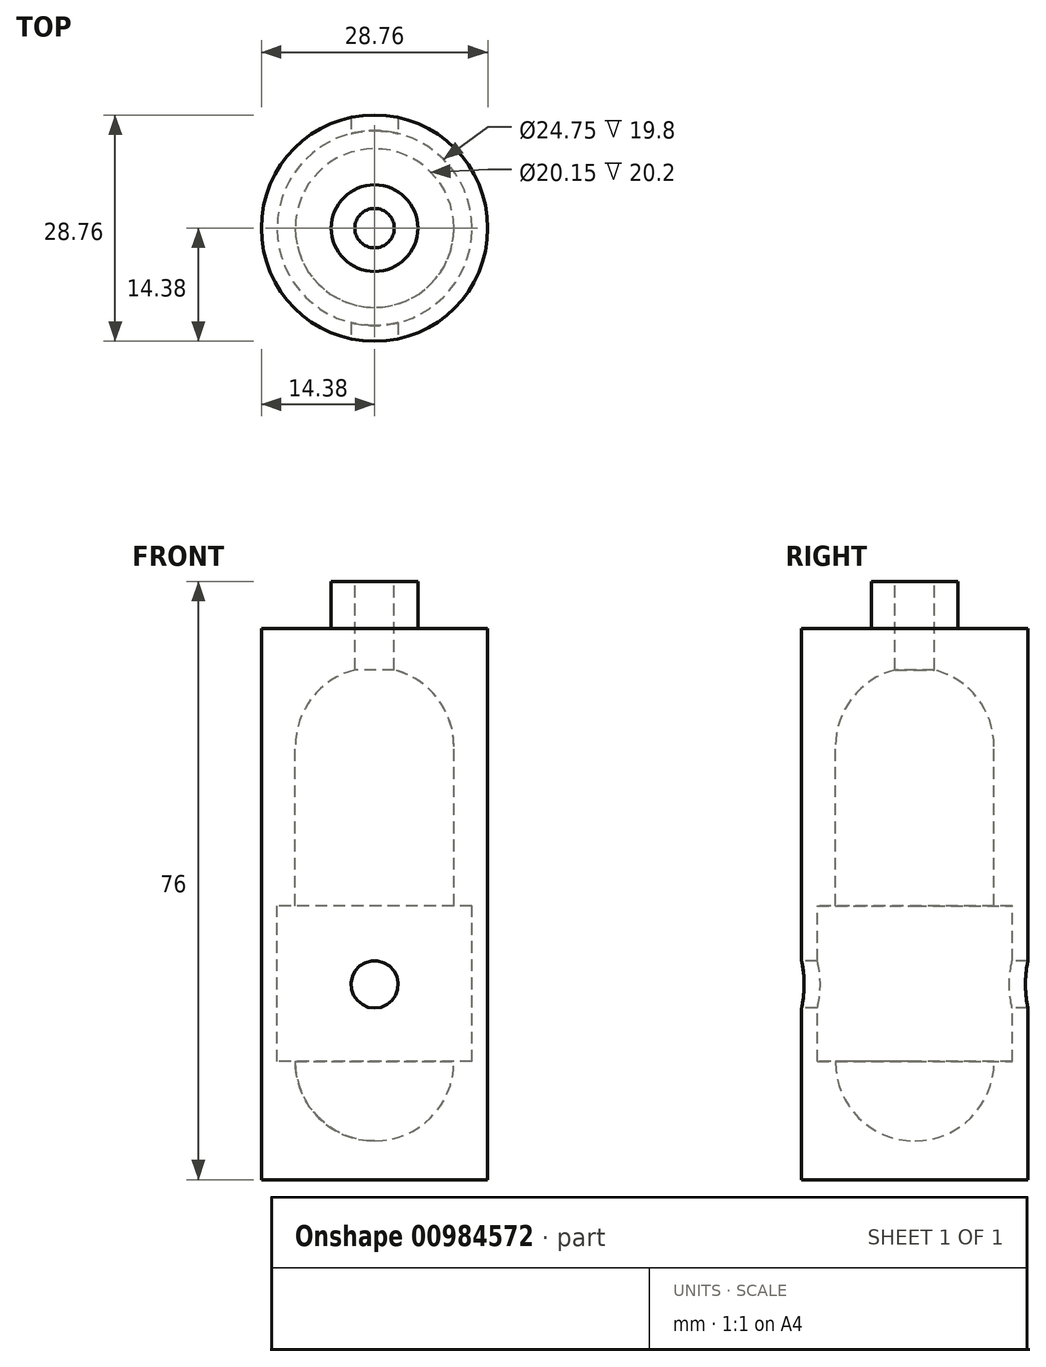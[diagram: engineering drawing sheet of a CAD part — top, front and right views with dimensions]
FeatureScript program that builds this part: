
annotation { "Feature Type Name" : "Feature", "Feature Type Description" : "" }
export const myFeature = defineFeature(function(context is Context, id is Id, definition is map)
    precondition{}
    {
        {
            var Q0;
            Q0=qCreatedBy(makeId("Front.planeOp"),FACE);
            var sketch = newSketch(context, id + "F0", { "sketchPlane" : qUnion([Q0])});
            skLineSegment(sketch, "E0.bottom", {"start": v(-14.37, 35) * mm, "end": v(14.37, 35) * mm});
            skLineSegment(sketch, "E0.top", {"start": v(-14.37, -35) * mm, "end": v(14.37, -35) * mm});
            skLineSegment(sketch, "E0.left", {"start": v(-14.37, 35) * mm, "end": v(-14.37, -35) * mm});
            skLineSegment(sketch, "E0.right", {"start": v(14.37, 35) * mm, "end": v(14.37, -35) * mm});
            skPoint(sketch, "E0.middle", {"position": v(0, 0) * mm});
            skLineSegment(sketch, "E1.bottom", {"start": v(-10.07, 20) * mm, "end": v(10.07, 20) * mm});
            skLineSegment(sketch, "E1.top", {"start": v(-10.08, -20) * mm, "end": v(10.07, -20) * mm});
            skLineSegment(sketch, "E1.left", {"start": v(-10.07, 20) * mm, "end": v(-10.07, -20) * mm});
            skLineSegment(sketch, "E1.right", {"start": v(10.07, 20) * mm, "end": v(10.07, -20) * mm});
            skCircle(sketch, "E2", {"center": v(0, 20) * mm, "radius": 10.07 * mm});
            skCircle(sketch, "E3", {"center": v(0, -20) * mm, "radius": 10.07 * mm});
            skLineSegment(sketch, "E4.bottom", {"start": v(12.37, -20) * mm, "end": v(-12.38, -20) * mm});
            skLineSegment(sketch, "E4.top", {"start": v(12.37, -0.2) * mm, "end": v(-12.38, -0.2) * mm});
            skLineSegment(sketch, "E4.left", {"start": v(12.37, -20) * mm, "end": v(12.37, -0.2) * mm});
            skLineSegment(sketch, "E4.right", {"start": v(-12.37, -20) * mm, "end": v(-12.37, -0.2) * mm});
            skLineSegment(sketch, "E5", {"start": v(0, 35) * mm, "end": v(0, -35) * mm});
            skLineSegment(sketch, "E6.bottom", {"start": v(2.5, 29.76) * mm, "end": v(-2.5, 29.76) * mm});
            skLineSegment(sketch, "E6.top", {"start": v(2.5, 35) * mm, "end": v(-2.5, 35) * mm});
            skLineSegment(sketch, "E6.left", {"start": v(2.5, 29.76) * mm, "end": v(2.5, 35) * mm});
            skLineSegment(sketch, "E6.right", {"start": v(-2.5, 29.76) * mm, "end": v(-2.5, 35) * mm});
            skPoint(sketch, "E6.middle", {"position": v(0, 32.38) * mm});
            skLineSegment(sketch, "E7.top", {"start": v(2.5, 41) * mm, "end": v(-2.5, 41) * mm});
            skLineSegment(sketch, "E7.left", {"start": v(2.5, 35) * mm, "end": v(2.5, 41) * mm});
            skLineSegment(sketch, "E7.right", {"start": v(-2.5, 35) * mm, "end": v(-2.5, 41) * mm});
            skLineSegment(sketch, "E8.bottom", {"start": v(-5.5, 35) * mm, "end": v(5.5, 35) * mm});
            skLineSegment(sketch, "E8.top", {"start": v(-5.5, 41) * mm, "end": v(5.5, 41) * mm});
            skLineSegment(sketch, "E8.left", {"start": v(-5.5, 35) * mm, "end": v(-5.5, 41) * mm});
            skLineSegment(sketch, "E8.right", {"start": v(5.5, 35) * mm, "end": v(5.5, 41) * mm});
            skLineSegment(sketch, "E9", {"start": v(0, 35) * mm, "end": v(0, 41) * mm});
            skSolve(sketch);
        }
        {
            var Q0;
            {var subQ3=sQuery(id+"F0.wireOp",EDGE,"E6.right");Q0=makeQuery(id+"F0.imprint","IMPRINT",FACE,{"disambiguationData":[TD([[makeQuery(id+"F0.imprint","IMPRINT",EDGE,{"derivedFrom":subQ3}),1.0]])]});}
            var Q1;
            {var subQ0=sQuery(id+"F0.wireOp",EDGE,"E7.right");Q1=makeQuery(id+"F0.imprint","IMPRINT",FACE,{"disambiguationData":[TD([[makeQuery(id+"F0.imprint","IMPRINT",EDGE,{"derivedFrom":subQ0}),1.0]])]});}
            var Q2;
            {var subQ7=sQuery(id+"F0.wireOp",EDGE,"E0.left");var subQ8=sQuery(id+"F0.wireOp",EDGE,"E0.top");var subQ9=makeQuery(id+"F0.imprint","INTERSECT",VERTEX,{"derivedFrom":[subQ8,subQ7]});Q2=makeQuery(id+"F0.imprint","IMPRINT",FACE,{"disambiguationData":[TD([[makeQuery(id+"F0.imprint","IMPRINT",EDGE,{"disambiguationData":[TD([[subQ9,-1.0]])],"derivedFrom":subQ8}),1.0]])]});}
            var Q3;
            {var subQ0=sQuery(id+"F0.wireOp",EDGE,"dL1wPY8W-PU4F-eiZV-HZuD-wuCvF6N1PBPw");var subQ1=sQuery(id+"F0.wireOp",EDGE,"E4.right");var subQ2=makeQuery(id+"F0.imprint","INTERSECT",VERTEX,{"derivedFrom":[subQ1,subQ0]});Q3=makeQuery(id+"F0.imprint","IMPRINT",FACE,{"disambiguationData":[TD([[makeQuery(id+"F0.imprint","IMPRINT",EDGE,{"disambiguationData":[TD([[subQ2,-1.0]])],"derivedFrom":subQ1}),1.0]])]});}
            var Q4;
            {var subQ0=sQuery(id+"F0.wireOp",EDGE,"QxNyx58Z-iYlF-um1u-wCvb-W1FFIKcIMJ6b.top");var subQ1=sQuery(id+"F0.wireOp",EDGE,"E4.right");var subQ2=makeQuery(id+"F0.imprint","INTERSECT",VERTEX,{"derivedFrom":[subQ1,subQ0]});Q4=makeQuery(id+"F0.imprint","IMPRINT",FACE,{"disambiguationData":[TD([[makeQuery(id+"F0.imprint","IMPRINT",EDGE,{"disambiguationData":[TD([[subQ2,-1.0]])],"derivedFrom":subQ1}),1.0]])]});}
            var Q5;
            Q5=sQuery(id+"F0.wireOp",EDGE,"E5");
            revolve(context, id + "F1", {"surfaceOperationType" : NewSurfaceOperationType.NEW, "entities" : qUnion([Q0, Q1, Q2, Q3, Q4]), "axis" : qUnion([Q5]), "revolveType" : RevolveType.FULL});
        }
        {
            var Q0;
            Q0=qCreatedBy(makeId("Front.planeOp"),FACE);
            var sketch = newSketch(context, id + "F2", { "sketchPlane" : qUnion([Q0])});
            skCircle(sketch, "E10", {"center": v(0, -10.2) * mm, "radius": 3 * mm});
            skSolve(sketch);
        }
        {
            var Q0;
            Q0 = qSketchRegion(id + "F2", true);
            extrude(context, id + "F3", {"entities" : qUnion([Q0]), "operationType" : NewBodyOperationType.REMOVE, "endBound" : BoundingType.SYMMETRIC, "oppositeDirection" : true, "depth" : 30 * mm, "offsetDistance" : 25 * mm});
        }
    });
